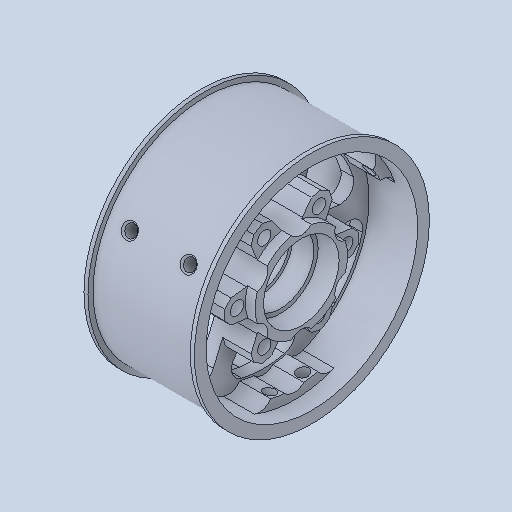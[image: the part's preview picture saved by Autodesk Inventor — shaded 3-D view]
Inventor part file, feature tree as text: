
AUTODESK INVENTOR PART (.ipt)
format: ipt  version: 2023 (Build 270158000, 158)  size: 356,864 bytes
history: native  units: in
note: dims shown in document units (in); Inventor stores cm internally (conversion verified against a paired STEP export)
features: mirror x1
ambient origin geometry x8: Origin, YZ Plane, XZ Plane, XY Plane, X Axis, Y Axis, Z Axis, Center Point
bodies: Solid1 (feature_tree)
feature tree (1):
  mirror  "Mirror3"
